AUTODESK INVENTOR PART (.ipt)
format: ipt  version: 2022 (Build 260153000, 153)  size: 350,720 bytes
history: native  units: in
note: dims shown in document units (in); Inventor stores cm internally (conversion verified against a paired STEP export)
features: extrude x2, sketch x2, other x1
ambient origin geometry x8: Origin, YZ Plane, XZ Plane, XY Plane, X Axis, Y Axis, Z Axis, Center Point
bodies: Body1 (feature_tree)
feature tree (5):
  other  "Sólido1"
  extrude  "Extrusión1"  Depth=0.2559in TaperAngle=0.0deg
  extrude  "Extrusión2"  Depth=0.0315in TaperAngle=0.0deg
  sketch  "Boceto1"  dims[d1=0.0787in d2=0.0394in d3=0.2559in d4=0.0in]
  sketch  "Boceto2"  dims[d7=0.1634in d8=0.4055in d9=0.1496in d10=0.0709in d11=0.4331in d12=0.2756in d13=0.0787in d14=0.0315in d15=0.0in]
